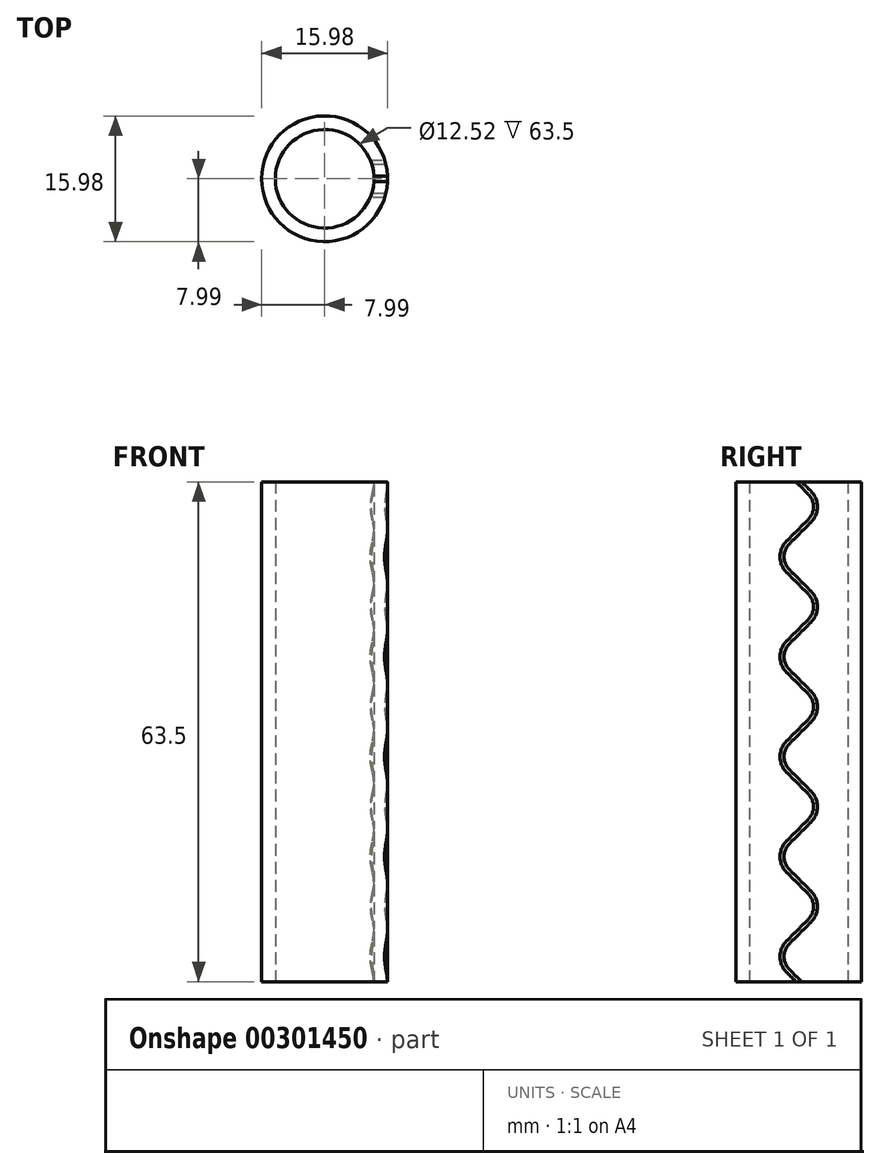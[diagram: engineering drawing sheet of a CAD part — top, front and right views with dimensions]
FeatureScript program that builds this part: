
annotation { "Feature Type Name" : "Feature", "Feature Type Description" : "" }
export const myFeature = defineFeature(function(context is Context, id is Id, definition is map)
    precondition{}
    {
        {
            var Q0;
            Q0=qCreatedBy(makeId("Top.planeOp"),FACE);
            var sketch = newSketch(context, id + "F0", { "sketchPlane" : qUnion([Q0])});
            skCircle(sketch, "E0", {"center": v(0, 0) * mm, "radius": 6.26 * mm});
            skCircle(sketch, "E1", {"center": v(0, 0) * mm, "radius": 7.99 * mm});
            skSolve(sketch);
        }
        {
            var Q0;
            Q0 = qSketchRegion(id + "F0", true);
            extrude(context, id + "F1", {"entities" : qUnion([Q0]), "depth" : 63.5 * mm});
        }
        {
            var Q0;
            Q0=makeQuery(id+"F1.opExtrude","CAP_FACE",FACE,{"disambiguationData":[OSD([sQuery(id+"F0.wireOp",EDGE,"E0"),sQuery(id+"F0.wireOp",EDGE,"E1")])],"isStart":false});
            var sketch = newSketch(context, id + "F2", { "sketchPlane" : qUnion([Q0])});
            skLineSegment(sketch, "E2", {"start": v(6.26, 0) * mm, "end": v(7.99, 0) * mm});
            skLineSegment(sketch, "E3", {"start": v(7.12, 0) * mm, "end": v(7.12, 3.61) * mm});
            skSolve(sketch);
        }
        {
            var Q0;
            Q0=qCreatedBy(makeId("Right.planeOp"),FACE);
            var Q1;
            Q1=sQuery(id+"F2.wireOp",VERTEX,"E3.end");
            cPlane(context, id + "F3", {"entities" : qUnion([Q0, Q1]), "cplaneType" : CPlaneType.PLANE_POINT, "offset" : 25.4 * mm, "width" : 152.4 * mm, "height" : 152.4 * mm});
        }
        {
            var Q0;
            Q0=qCreatedBy(id+"F3.planeOp",FACE);
            var sketch = newSketch(context, id + "F4", { "sketchPlane" : qUnion([Q0])});
            skLineSegment(sketch, "E4", {"start": v(0, 63.5) * mm, "end": v(1.38, 62.12) * mm});
            skLineSegment(sketch, "E5", {"start": v(1.38, 58.53) * mm, "end": v(0, 57.15) * mm});
            skLineSegment(sketch, "E6", {"start": v(0, 57.15) * mm, "end": v(-1.38, 55.77) * mm});
            skLineSegment(sketch, "E7", {"start": v(-1.38, 52.18) * mm, "end": v(0, 50.8) * mm});
            skLineSegment(sketch, "E8.0.1.0", {"start": v(-1.38, 39.48) * mm, "end": v(0, 38.1) * mm});
            skLineSegment(sketch, "E8.0.1.1", {"start": v(1.38, 45.83) * mm, "end": v(0, 44.45) * mm});
            skLineSegment(sketch, "E8.0.1.2", {"start": v(0, 44.45) * mm, "end": v(-1.38, 43.07) * mm});
            skLineSegment(sketch, "E8.0.1.3", {"start": v(0, 50.8) * mm, "end": v(1.38, 49.42) * mm});
            skLineSegment(sketch, "E8.direction1", {"start": v(0, 50.8) * mm, "end": v(-23.11, 50.8) * mm, "construction": true});
            skLineSegment(sketch, "E8.direction2", {"start": v(0, 50.8) * mm, "end": v(0, 38.1) * mm, "construction": true});
            skPoint(sketch, "E9.visualSharp", {"position": v(-3.18, 53.98) * mm});
            skArc(sketch, "E9.filletArc", {"start": v(-1.38, 55.77) * mm, "mid": v(-2.12, 53.97) * mm, "end": v(-1.38, 52.18) * mm});
            skPoint(sketch, "E10.visualSharp", {"position": v(3.18, 47.62) * mm});
            skArc(sketch, "E10.filletArc", {"start": v(1.38, 45.83) * mm, "mid": v(2.12, 47.62) * mm, "end": v(1.38, 49.42) * mm});
            skPoint(sketch, "E11.visualSharp", {"position": v(3.17, 60.32) * mm});
            skArc(sketch, "E11.filletArc", {"start": v(1.38, 58.53) * mm, "mid": v(2.12, 60.33) * mm, "end": v(1.38, 62.12) * mm});
            skPoint(sketch, "E12.visualSharp", {"position": v(-3.18, 41.27) * mm});
            skArc(sketch, "E12.filletArc", {"start": v(-1.38, 43.07) * mm, "mid": v(-2.12, 41.27) * mm, "end": v(-1.38, 39.48) * mm});
            skLineSegment(sketch, "E13.0.1.0", {"start": v(-1.38, 26.78) * mm, "end": v(0, 25.4) * mm});
            skArc(sketch, "E13.0.1.1", {"start": v(-1.38, 30.37) * mm, "mid": v(-2.12, 28.57) * mm, "end": v(-1.38, 26.78) * mm});
            skLineSegment(sketch, "E13.0.1.2", {"start": v(0, 31.75) * mm, "end": v(-1.38, 30.37) * mm});
            skLineSegment(sketch, "E13.0.1.3", {"start": v(1.38, 33.13) * mm, "end": v(0, 31.75) * mm});
            skArc(sketch, "E13.0.1.4", {"start": v(1.38, 33.13) * mm, "mid": v(2.12, 34.92) * mm, "end": v(1.38, 36.72) * mm});
            skLineSegment(sketch, "E13.0.1.5", {"start": v(0, 38.1) * mm, "end": v(1.38, 36.72) * mm});
            skLineSegment(sketch, "E13.0.2.0", {"start": v(-1.38, 14.08) * mm, "end": v(0, 12.7) * mm});
            skArc(sketch, "E13.0.2.1", {"start": v(-1.38, 17.67) * mm, "mid": v(-2.12, 15.87) * mm, "end": v(-1.38, 14.08) * mm});
            skLineSegment(sketch, "E13.0.2.2", {"start": v(0, 19.05) * mm, "end": v(-1.38, 17.67) * mm});
            skLineSegment(sketch, "E13.0.2.3", {"start": v(1.38, 20.43) * mm, "end": v(0, 19.05) * mm});
            skArc(sketch, "E13.0.2.4", {"start": v(1.38, 20.43) * mm, "mid": v(2.12, 22.22) * mm, "end": v(1.38, 24.02) * mm});
            skLineSegment(sketch, "E13.0.2.5", {"start": v(0, 25.4) * mm, "end": v(1.38, 24.02) * mm});
            skLineSegment(sketch, "E13.0.3.0", {"start": v(-1.38, 1.38) * mm, "end": v(0, 0) * mm});
            skArc(sketch, "E13.0.3.1", {"start": v(-1.38, 4.97) * mm, "mid": v(-2.12, 3.17) * mm, "end": v(-1.38, 1.38) * mm});
            skLineSegment(sketch, "E13.0.3.2", {"start": v(0, 6.35) * mm, "end": v(-1.38, 4.97) * mm});
            skLineSegment(sketch, "E13.0.3.3", {"start": v(1.38, 7.73) * mm, "end": v(0, 6.35) * mm});
            skArc(sketch, "E13.0.3.4", {"start": v(1.38, 7.73) * mm, "mid": v(2.12, 9.52) * mm, "end": v(1.38, 11.32) * mm});
            skLineSegment(sketch, "E13.0.3.5", {"start": v(0, 12.7) * mm, "end": v(1.38, 11.32) * mm});
            skLineSegment(sketch, "E13.direction1", {"start": v(0, 38.1) * mm, "end": v(-25.4, 38.1) * mm, "construction": true});
            skLineSegment(sketch, "E13.direction2", {"start": v(0, 38.1) * mm, "end": v(0, 25.4) * mm, "construction": true});
            skLineSegment(sketch, "E14", {"start": v(0, 0) * mm, "end": v(1.38, -1.38) * mm});
            skLineSegment(sketch, "E15", {"start": v(0, 63.5) * mm, "end": v(-1.38, 64.88) * mm});
            skSolve(sketch);
        }
        {
            var Q0;
            Q0=sQuery(id+"F4.wireOp",VERTEX,"E14.end");
            var Q1;
            Q1=sQuery(id+"F4.wireOp",EDGE,"E14");
            cPlane(context, id + "F5", {"entities" : qUnion([Q0, Q1]), "cplaneType" : CPlaneType.CURVE_POINT, "offset" : 25.4 * mm, "width" : 152.4 * mm, "height" : 152.4 * mm});
        }
        {
            var Q0;
            Q0=qCreatedBy(id+"F5.planeOp",FACE);
            var sketch = newSketch(context, id + "F6", { "sketchPlane" : qUnion([Q0])});
            skLineSegment(sketch, "E16", {"start": v(-7.76, -0.25) * mm, "end": v(-6.49, -0.25) * mm});
            skLineSegment(sketch, "E17", {"start": v(-7.76, -0.25) * mm, "end": v(-9.84, -0.25) * mm});
            skLineSegment(sketch, "E18", {"start": v(-9.84, -0.25) * mm, "end": v(-9.84, 0.25) * mm});
            skLineSegment(sketch, "E19", {"start": v(-9.84, 0.25) * mm, "end": v(-7.76, 0.25) * mm});
            skLineSegment(sketch, "E20", {"start": v(-7.76, 0.25) * mm, "end": v(-6.49, 0.25) * mm});
            skLineSegment(sketch, "E21", {"start": v(-6.49, 0.25) * mm, "end": v(-4.4, 0.25) * mm});
            skLineSegment(sketch, "E22", {"start": v(-4.4, 0.25) * mm, "end": v(-4.4, -0.25) * mm});
            skLineSegment(sketch, "E23", {"start": v(-4.4, -0.25) * mm, "end": v(-6.49, -0.25) * mm});
            skLineSegment(sketch, "E24", {"start": v(-7.12, 0) * mm, "end": v(-7.12, -0.25) * mm, "construction": true});
            skLineSegment(sketch, "E25", {"start": v(-7.12, 0) * mm, "end": v(-7.12, 0.25) * mm, "construction": true});
            skLineSegment(sketch, "E26", {"start": v(-7.12, 0) * mm, "end": v(-7.76, 0) * mm, "construction": true});
            skSolve(sketch);
        }
        {
            var Q0;
            Q0 = qSketchRegion(id + "F6", true);
            var Q1;
            Q1 = qConstructionFilter(qBodyType(qCreatedBy(id + "F4" ,EDGE), BodyType.WIRE), ConstructionObject.NO);
            sweep(context, id + "F7", {"operationType" : NewBodyOperationType.REMOVE, "profiles" : qUnion([Q0]), "path" : qUnion([Q1])});
        }
    });
